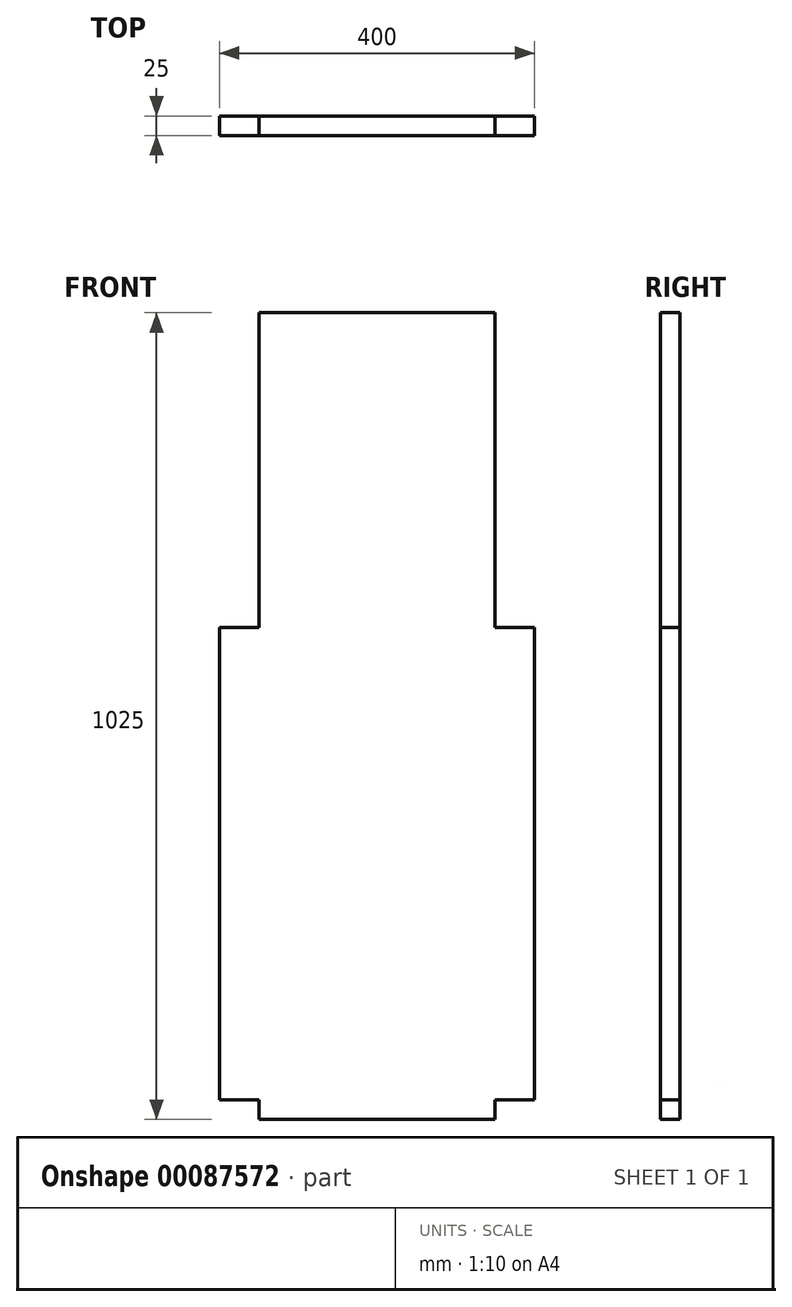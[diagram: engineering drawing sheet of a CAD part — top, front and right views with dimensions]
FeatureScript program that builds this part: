
annotation { "Feature Type Name" : "Feature", "Feature Type Description" : "" }
export const myFeature = defineFeature(function(context is Context, id is Id, definition is map)
    precondition{}
    {
        {
            var Q0;
            Q0=qCreatedBy(makeId("Front.planeOp"),FACE);
            var sketch = newSketch(context, id + "F0", { "sketchPlane" : qUnion([Q0])});
            skLineSegment(sketch, "E0.bottom", {"start": v(-400, 600) * mm, "end": v(-350, 600) * mm});
            skLineSegment(sketch, "E0.top", {"start": v(-400, 0) * mm, "end": v(-350, 0) * mm});
            skLineSegment(sketch, "E0.left", {"start": v(-400, 600) * mm, "end": v(-400, 0) * mm});
            skLineSegment(sketch, "E0.right", {"start": v(0, 600) * mm, "end": v(0, 0) * mm});
            skLineSegment(sketch, "E1.top", {"start": v(-350, 1000) * mm, "end": v(-50, 1000) * mm});
            skLineSegment(sketch, "E1.left", {"start": v(-350, 600) * mm, "end": v(-350, 1000) * mm});
            skLineSegment(sketch, "E1.right", {"start": v(-50, 600) * mm, "end": v(-50, 1000) * mm});
            skLineSegment(sketch, "E2.top", {"start": v(-350, -25) * mm, "end": v(-50, -25) * mm});
            skLineSegment(sketch, "E2.left", {"start": v(-350, 0) * mm, "end": v(-350, -25) * mm});
            skLineSegment(sketch, "E2.right", {"start": v(-50, 0) * mm, "end": v(-50, -25) * mm});
            skLineSegment(sketch, "E3.trimOffspring", {"start": v(-50, 0) * mm, "end": v(0, 0) * mm});
            skLineSegment(sketch, "E4.trimOffspring", {"start": v(-50, 600) * mm, "end": v(0, 600) * mm});
            skSolve(sketch);
        }
        {
            var Q0;
            Q0=makeQuery(id+"F0.imprint","IMPRINT",FACE,{"disambiguationData":[TD([[makeQuery(id+"F0.imprint","IMPRINT",EDGE,{"derivedFrom":sQuery(id+"F0.wireOp",EDGE,"E0.bottom")}),-1.0]])]});
            extrude(context, id + "F1", {"entities" : qUnion([Q0]), "depth" : 25 * mm});
        }
    });
